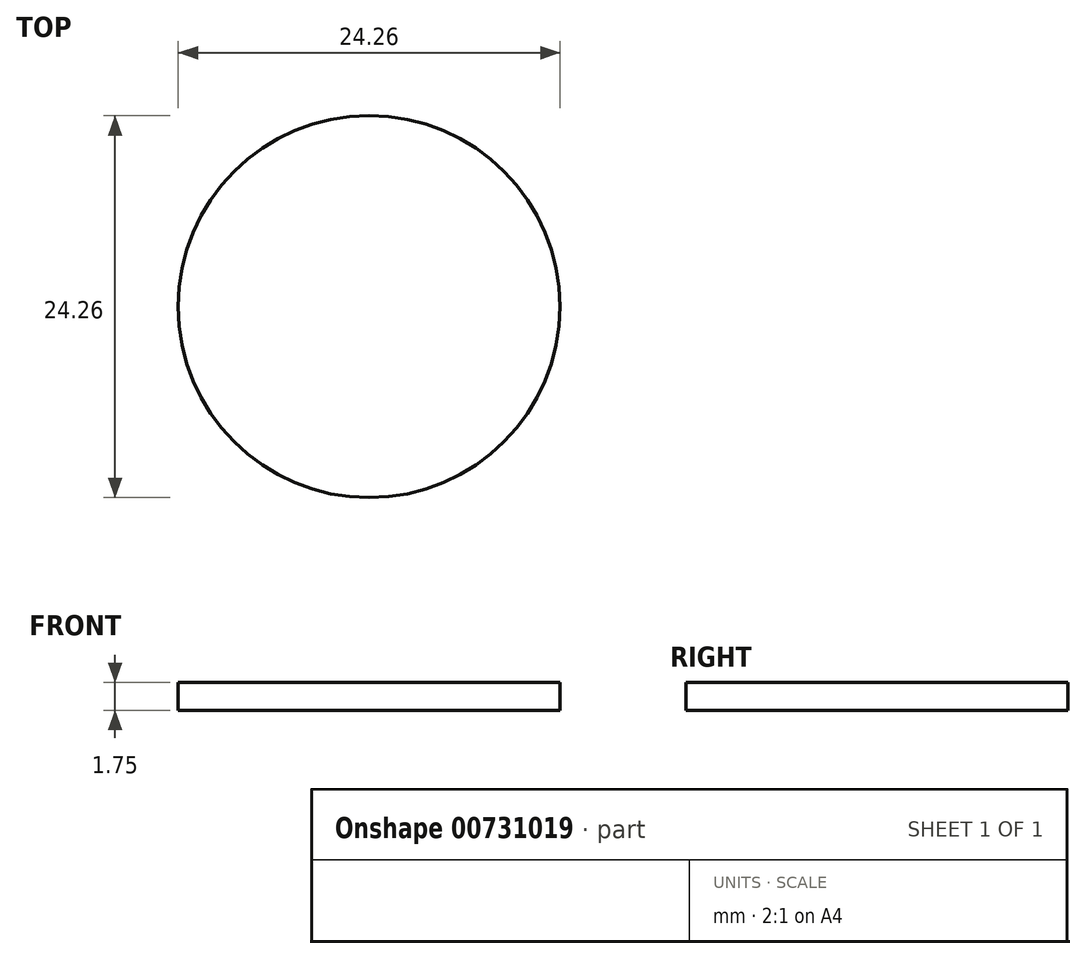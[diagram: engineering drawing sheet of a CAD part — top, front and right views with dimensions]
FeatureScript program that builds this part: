
annotation { "Feature Type Name" : "Feature", "Feature Type Description" : "" }
export const myFeature = defineFeature(function(context is Context, id is Id, definition is map)
    precondition{}
    {
        {
            var Q0;
            Q0=qCreatedBy(makeId("Top.planeOp"),FACE);
            var sketch = newSketch(context, id + "F0", { "sketchPlane" : qUnion([Q0])});
            skCircle(sketch, "E0", {"center": v(0, 0) * mm, "radius": 12.13 * mm});
            skSolve(sketch);
        }
        {
            var Q0;
            Q0=makeQuery(id+"F0.imprint","IMPRINT",FACE,{"disambiguationData":[TD([[makeQuery(id+"F0.imprint","IMPRINT",EDGE,{"derivedFrom":sQuery(id+"F0.wireOp",EDGE,"E0")}),1.0]])]});
            extrude(context, id + "F1", {"entities" : qUnion([Q0]), "depth" : 1.75 * mm, "offsetDistance" : 25 * mm});
        }
    });
